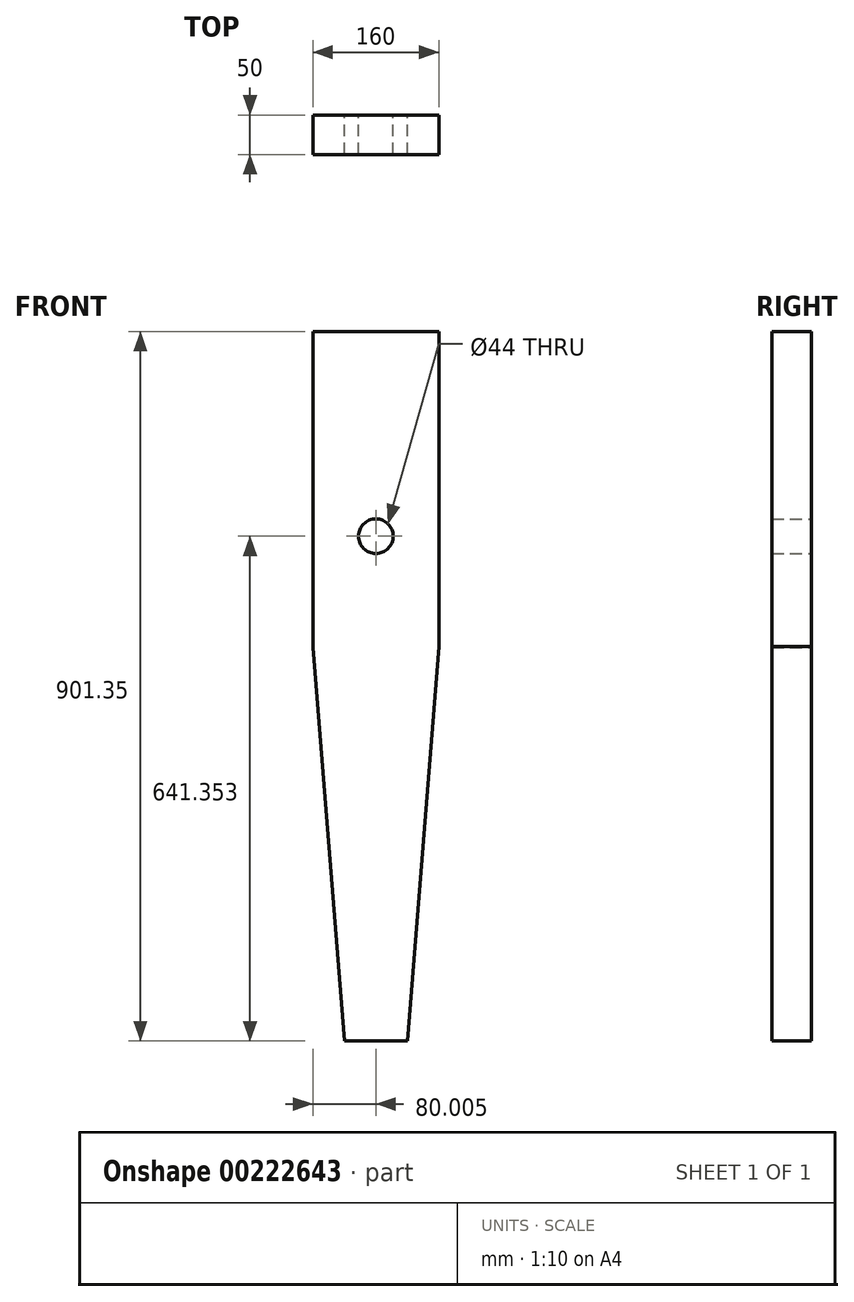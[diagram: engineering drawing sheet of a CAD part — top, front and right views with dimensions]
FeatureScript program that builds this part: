
annotation { "Feature Type Name" : "Feature", "Feature Type Description" : "" }
export const myFeature = defineFeature(function(context is Context, id is Id, definition is map)
    precondition{}
    {
        {
            var Q0;
            Q0=qCreatedBy(makeId("Front.planeOp"),FACE);
            var sketch = newSketch(context, id + "F0", { "sketchPlane" : qUnion([Q0])});
            skLineSegment(sketch, "E0.bottom", {"start": v(-77.28, 255.52) * mm, "end": v(82.72, 255.52) * mm});
            skLineSegment(sketch, "E0.left", {"start": v(-77.28, 255.52) * mm, "end": v(-77.28, -145.83) * mm});
            skLineSegment(sketch, "E0.right", {"start": v(82.72, 255.52) * mm, "end": v(82.72, -144.48) * mm});
            skPoint(sketch, "E1.end.orphan", {"position": v(2.72, 255.52) * mm});
            skCircle(sketch, "E2", {"center": v(2.72, -4.48) * mm, "radius": 22 * mm});
            skLineSegment(sketch, "E3", {"start": v(42.62, -645.83) * mm, "end": v(82.72, -144.48) * mm});
            skLineSegment(sketch, "E4", {"start": v(-37.28, -645.83) * mm, "end": v(-77.28, -145.83) * mm});
            skLineSegment(sketch, "E5", {"start": v(-37.28, -645.83) * mm, "end": v(42.62, -645.83) * mm});
            skSolve(sketch);
        }
        {
            var Q0;
            {var subQ5=sQuery(id+"F0.wireOp",EDGE,"E0.top");Q0=makeQuery(id+"F0.imprint","IMPRINT",FACE,{"disambiguationData":[TD([[makeQuery(id+"F0.imprint","IMPRINT",EDGE,{"derivedFrom":subQ5}),1.0]])]});}
            var Q1;
            Q1=makeQuery(id+"F0.imprint","IMPRINT",FACE,{"disambiguationData":[TD([[makeQuery(id+"F0.imprint","IMPRINT",EDGE,{"derivedFrom":sQuery(id+"F0.wireOp",EDGE,"E0.bottom")}),-1.0]])]});
            extrude(context, id + "F1", {"entities" : qUnion([Q0, Q1]), "depth" : 50 * mm});
        }
    });
